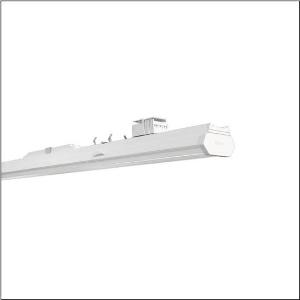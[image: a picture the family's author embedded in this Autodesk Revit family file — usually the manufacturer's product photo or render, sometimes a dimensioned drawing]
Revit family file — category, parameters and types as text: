
# Revit family: licross_r__21_protected_ho_52td12dn4dxm_7c2c
name_source: partatom
category: Lighting Fixtures
units: mm (PartAtom-declared; Revit-internal decimal feet)

## family parameters
Cut with Voids When Loaded = No
Host = Face
Light Source = No
Part Type = Normal
Room Calculation Point = No
Round Connector Dimension = Use Diameter
Shared = No

## types (1)
- --- (1 x LED, 13000 lm, 74.3 W, 4000K)
    Apparent Load = 74 VA
    CIE Flux Codes = 70 91 97 98 100
    Color Rendering = 80
    Color Temperature = 4000K
    Default Elevation = 1800 mm
    Description = Licross® 21 Protected HO, luminaire insert, of sheet steel, galvanised, coil coated, white, length: 1.500mm, width: 90mm, height: 103mm, LED rated luminous flux: 13.000lm, light colour: 840, control gear: DALI 2, with plug, 5-pole, with phase selection, mains connection: 220..240V, AC, 50/60Hz, rated input power: 74W, halogen-free wiring, primary light control with lens, of plastic, primary optical cover: cover, of PMMA, light emission: direct distribution, primary light characteristic: symmetric, protection rating (complete): IP54, insulation class (complete): insulation class I (protective earthing), certification: CE, ENEC, VDE, UKCA, protection symbol: D if used in an environment with non-conductive dust loads with corresponding accessories, impact resistance: IK06, permissible ambient temperature for indoor applications: -25..+40°C, corresponds to IFS (International Featured Standards) requirements for safety and quality in the food industry, reducing of maximum allowable ambient temperature of 5°C with ceiling mounting, LABS conformity tested according to VDMA 24364:2018-05, packaging unit: 1 piece
    Height = 92 mm
    Lamp = 1 x LED
    Lamp Light Flux = 13000 lm
    Lamp Power = 74.3 W
    Lamp count = 1
    Length = 1500 mm
    Luminous efficacy = 175 lm/W
    Manufacturer = Siteco
    ModVariant = No
    Model = 52TD12DN4DXM
    Mounting Place = Ceiling
    Mounting Type = Pendant
    Number of Poles = 1
    OnlyDefault = Yes
    Power Factor = 1
    Product Name = Licross® 21 Protected HO
    Product group = luminaire insert
    ProductGroupID = 901
    Protection Class = Protection class I
    Protection Degree = IP 54
    RLX_Detail_Level = 1
    RLX_Emergency_Light_Flux = 0 lm
    RLX_Emergency_Type = 0
    RLX_Emergency_Type_DB = No
    RlxData = <blob elided: 24417 chars, md5=3a1aab3c>
    Socket = socket
    Standby Power = 0 W
    System Light Flux = 13000 lm
    System Power = 74 W
    Type Comments = factory setting: luminous flux: 100 % | dim-lin: 254 | 424 mA
    Type Image = l_1256148.jpg
    URL = http://relux.com
    VarID = @adj_078621
    Voltage = 0 V
    Weight = 0.00 kg
    Width = 88 mm

## geometry (parser evidence)
native form markers: Blend x4, Sweep x9
no freeform markers — native parametric forms only
